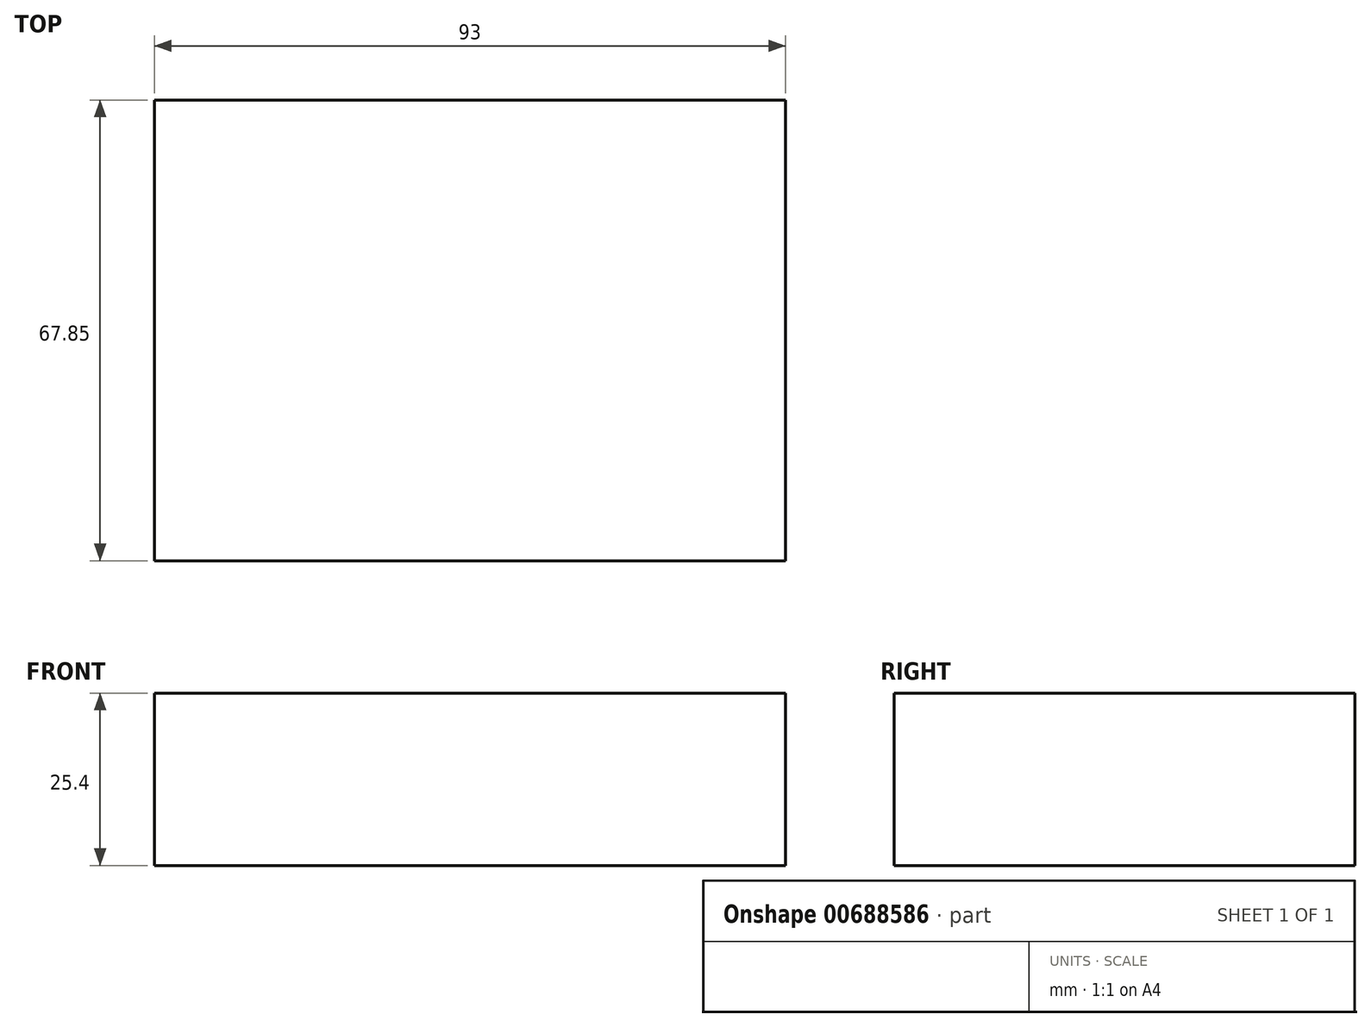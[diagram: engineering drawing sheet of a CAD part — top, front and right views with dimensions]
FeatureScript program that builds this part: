
annotation { "Feature Type Name" : "Feature", "Feature Type Description" : "" }
export const myFeature = defineFeature(function(context is Context, id is Id, definition is map)
    precondition{}
    {
        {
            var Q0;
            Q0=qCreatedBy(makeId("Top.planeOp"),FACE);
            var sketch = newSketch(context, id + "F0", { "sketchPlane" : qUnion([Q0])});
            skLineSegment(sketch, "E0.bottom", {"start": v(-142.1, 15.78) * mm, "end": v(-49.09, 15.78) * mm});
            skLineSegment(sketch, "E0.top", {"start": v(-142.1, -52.07) * mm, "end": v(-49.09, -52.07) * mm});
            skLineSegment(sketch, "E0.left", {"start": v(-142.1, 15.78) * mm, "end": v(-142.1, -52.07) * mm});
            skLineSegment(sketch, "E0.right", {"start": v(-49.09, 15.78) * mm, "end": v(-49.09, -52.07) * mm});
            skSolve(sketch);
        }
        {
            var Q0;
            Q0 = qSketchRegion(id + "F0", true);
            extrude(context, id + "F1", {"entities" : qUnion([Q0]), "depth" : 25.4 * mm, "offsetDistance" : 25.4 * mm});
        }
    });
